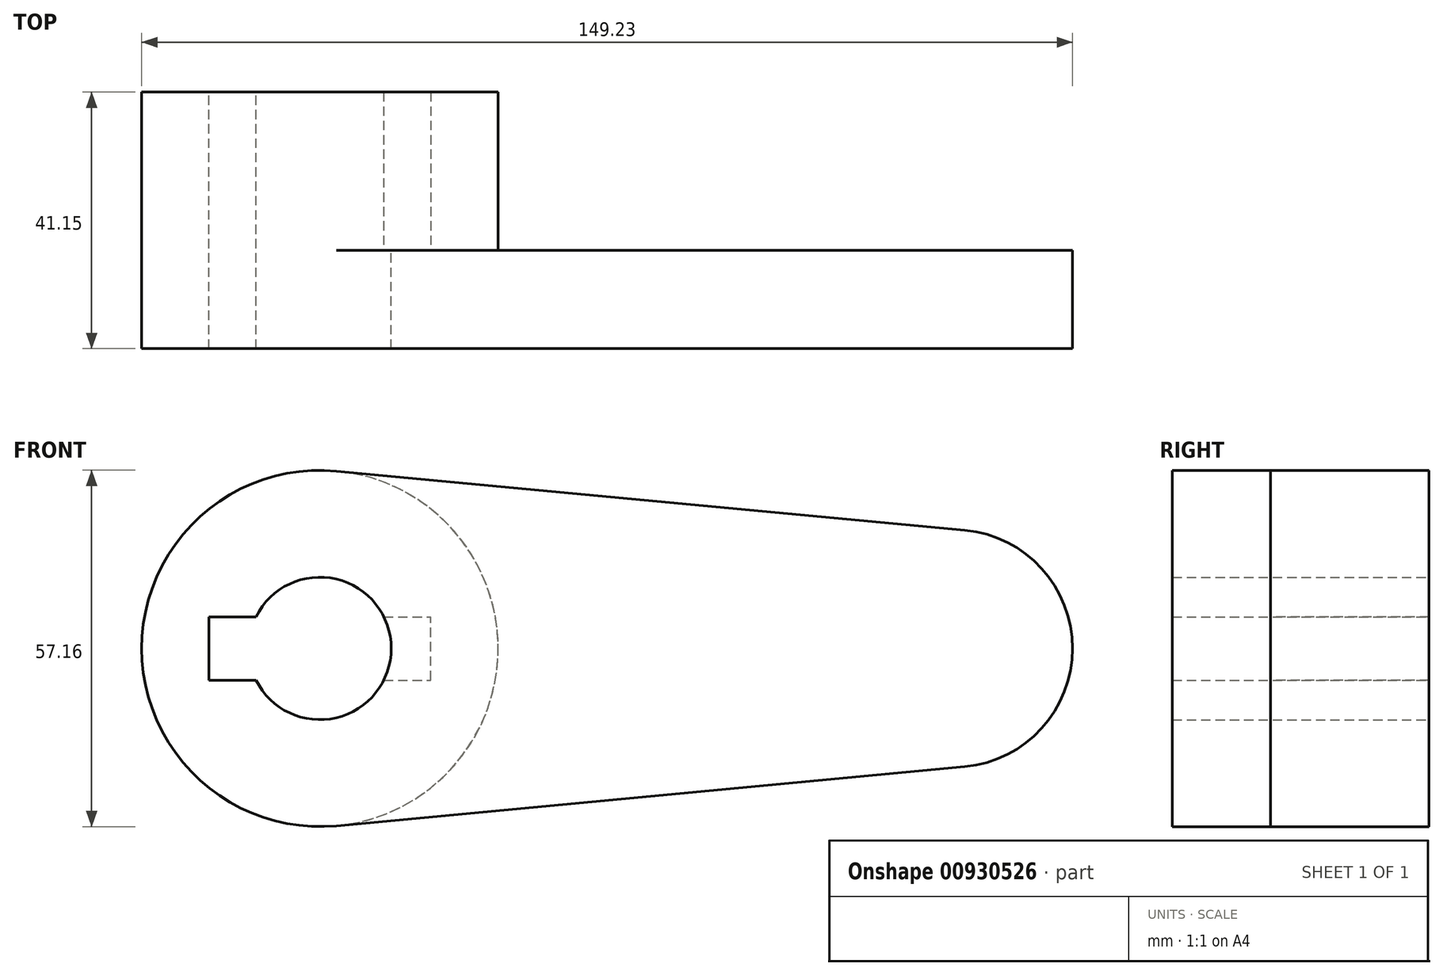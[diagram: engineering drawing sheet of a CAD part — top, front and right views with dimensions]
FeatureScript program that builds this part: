
annotation { "Feature Type Name" : "Feature", "Feature Type Description" : "" }
export const myFeature = defineFeature(function(context is Context, id is Id, definition is map)
    precondition{}
    {
        {
            var Q0;
            Q0=qCreatedBy(makeId("Front.planeOp"),FACE);
            var sketch = newSketch(context, id + "F0", { "sketchPlane" : qUnion([Q0])});
            skCircle(sketch, "E0", {"center": v(0, 0) * mm, "radius": 28.57 * mm});
            skCircle(sketch, "E1", {"center": v(101.6, 0) * mm, "radius": 19.05 * mm});
            skLineSegment(sketch, "E2", {"start": v(2.68, 28.45) * mm, "end": v(103.39, 18.97) * mm});
            skLineSegment(sketch, "E3", {"start": v(2.68, -28.45) * mm, "end": v(103.39, -18.97) * mm});
            skCircle(sketch, "E4", {"center": v(0, 0) * mm, "radius": 11.43 * mm});
            skCircle(sketch, "E5", {"center": v(101.6, 0) * mm, "radius": 11.43 * mm});
            skLineSegment(sketch, "E6.bottom", {"start": v(-17.78, -5.08) * mm, "end": v(17.78, -5.08) * mm});
            skLineSegment(sketch, "E6.top", {"start": v(-17.78, 5.08) * mm, "end": v(17.78, 5.08) * mm});
            skLineSegment(sketch, "E6.left", {"start": v(-17.78, -5.08) * mm, "end": v(-17.78, 5.08) * mm});
            skLineSegment(sketch, "E6.right", {"start": v(17.78, -5.08) * mm, "end": v(17.78, 5.08) * mm});
            skSolve(sketch);
        }
        {
            var Q0;
            {var subQ5=sQuery(id+"F0.wireOp",EDGE,"E6.right");Q0=makeQuery(id+"F0.imprint","IMPRINT",FACE,{"disambiguationData":[TD([[makeQuery(id+"F0.imprint","IMPRINT",EDGE,{"derivedFrom":subQ5}),1.0]])]});}
            var Q1;
            Q1=makeQuery(id+"F0.imprint","IMPRINT",FACE,{"disambiguationData":[TD([[makeQuery(id+"F0.imprint","IMPRINT",EDGE,{"derivedFrom":sQuery(id+"F0.wireOp",EDGE,"E5")}),1.0]])]});
            var Q2;
            {var subQ0=sQuery(id+"F0.wireOp",EDGE,"E2");Q2=makeQuery(id+"F0.imprint","IMPRINT",FACE,{"disambiguationData":[TD([[makeQuery(id+"F0.imprint","IMPRINT",EDGE,{"derivedFrom":subQ0}),-1.0]])]});}
            var Q3;
            {var subQ7=sQuery(id+"F0.wireOp",EDGE,"E6.left");Q3=makeQuery(id+"F0.imprint","IMPRINT",FACE,{"disambiguationData":[TD([[makeQuery(id+"F0.imprint","IMPRINT",EDGE,{"derivedFrom":subQ7}),1.0]])]});}
            var Q4;
            Q4=makeQuery(id+"F0.imprint","IMPRINT",FACE,{"disambiguationData":[TD([[makeQuery(id+"F0.imprint","IMPRINT",EDGE,{"derivedFrom":sQuery(id+"F0.wireOp",EDGE,"E5")}),-1.0]])]});
            extrude(context, id + "F1", {"entities" : qUnion([Q0, Q1, Q2, Q3, Q4]), "depth" : 15.75 * mm, "offsetDistance" : 25.4 * mm});
        }
        {
            var Q0;
            {var subQ7=sQuery(id+"F0.wireOp",EDGE,"E6.left");Q0=makeQuery(id+"F0.imprint","IMPRINT",FACE,{"disambiguationData":[TD([[makeQuery(id+"F0.imprint","IMPRINT",EDGE,{"derivedFrom":subQ7}),1.0]])]});}
            extrude(context, id + "F2", {"entities" : qUnion([Q0]), "operationType" : NewBodyOperationType.ADD, "oppositeDirection" : true, "depth" : 25.4 * mm, "offsetDistance" : 25.4 * mm});
        }
    });
